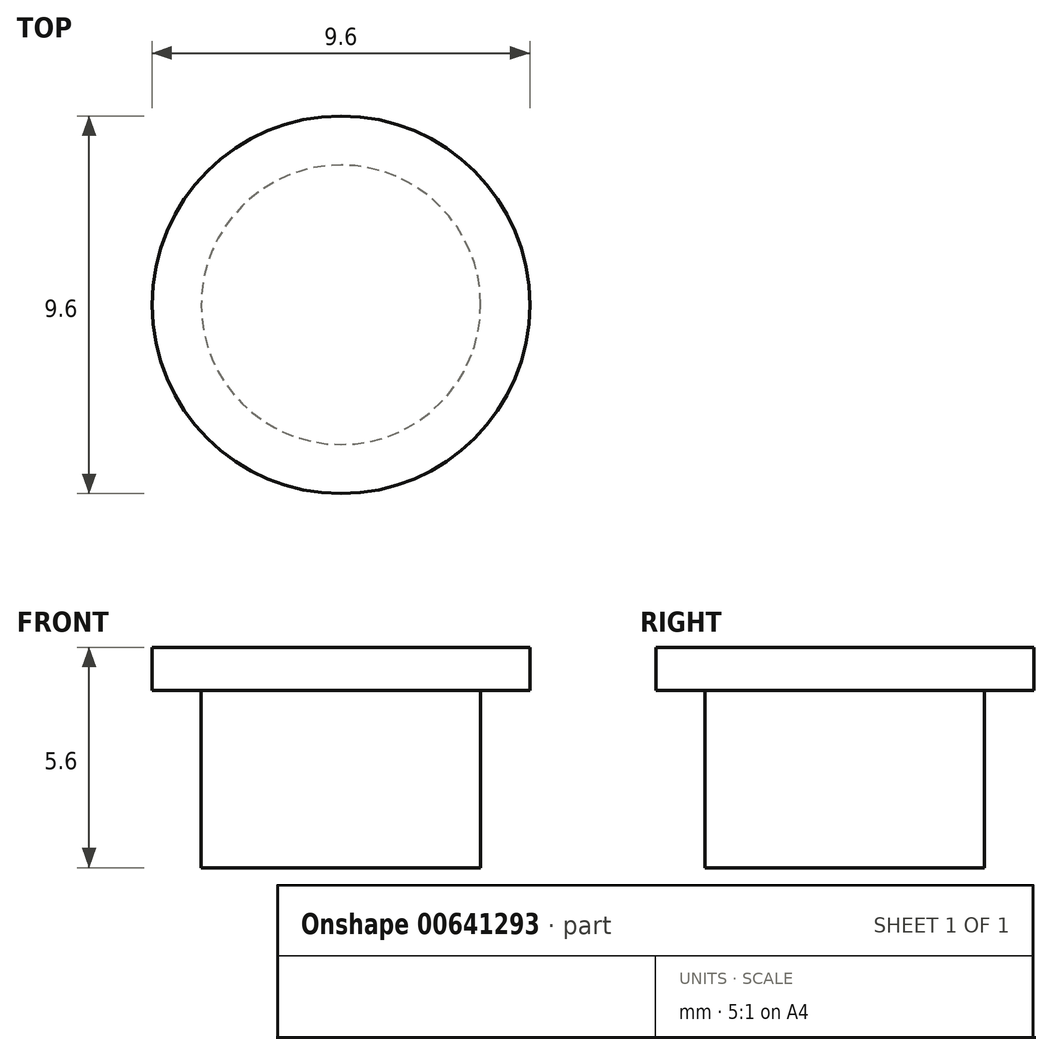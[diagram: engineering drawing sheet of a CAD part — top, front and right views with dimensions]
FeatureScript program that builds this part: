
annotation { "Feature Type Name" : "Feature", "Feature Type Description" : "" }
export const myFeature = defineFeature(function(context is Context, id is Id, definition is map)
    precondition{}
    {
        {
            var Q0;
            Q0=qCreatedBy(makeId("Top.planeOp"),FACE);
            var sketch = newSketch(context, id + "F0", { "sketchPlane" : qUnion([Q0])});
            skCircle(sketch, "E0", {"center": v(0, 0) * mm, "radius": 3.55 * mm});
            skCircle(sketch, "E1", {"center": v(0, 0) * mm, "radius": 4.8 * mm});
            skSolve(sketch);
        }
        {
            var Q0;
            Q0=makeQuery(id+"F0.imprint","IMPRINT",FACE,{"disambiguationData":[TD([[makeQuery(id+"F0.imprint","IMPRINT",EDGE,{"derivedFrom":sQuery(id+"F0.wireOp",EDGE,"E0")}),-1.0]])]});
            var Q1;
            Q1=makeQuery(id+"F0.imprint","IMPRINT",FACE,{"disambiguationData":[TD([[makeQuery(id+"F0.imprint","IMPRINT",EDGE,{"derivedFrom":sQuery(id+"F0.wireOp",EDGE,"E0")}),1.0]])]});
            extrude(context, id + "F1", {"entities" : qUnion([Q0, Q1]), "depth" : 1.1 * mm, "offsetDistance" : 25 * mm});
        }
        {
            var Q0;
            Q0=makeQuery(id+"F0.imprint","IMPRINT",FACE,{"disambiguationData":[TD([[makeQuery(id+"F0.imprint","IMPRINT",EDGE,{"derivedFrom":sQuery(id+"F0.wireOp",EDGE,"E0")}),1.0]])]});
            extrude(context, id + "F2", {"entities" : qUnion([Q0]), "operationType" : NewBodyOperationType.ADD, "oppositeDirection" : true, "depth" : 4.5 * mm, "offsetDistance" : 25 * mm});
        }
    });
